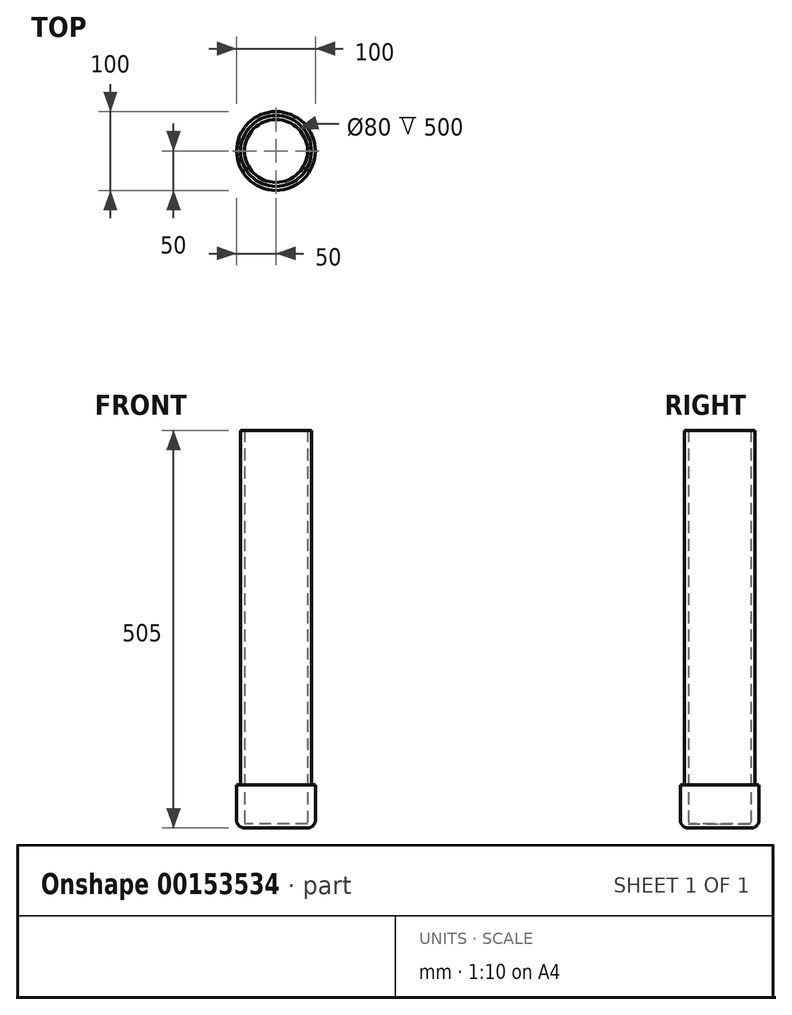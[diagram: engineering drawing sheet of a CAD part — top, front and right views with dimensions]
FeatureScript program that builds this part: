
annotation { "Feature Type Name" : "Feature", "Feature Type Description" : "" }
export const myFeature = defineFeature(function(context is Context, id is Id, definition is map)
    precondition{}
    {
        {
            var Q0;
            Q0=qCreatedBy(makeId("Top.planeOp"),FACE);
            var sketch = newSketch(context, id + "F0", { "sketchPlane" : qUnion([Q0])});
            skCircle(sketch, "E0", {"center": v(0, 0) * mm, "radius": 40 * mm});
            skCircle(sketch, "E1", {"center": v(0, 0) * mm, "radius": 50 * mm});
            skCircle(sketch, "E2", {"center": v(0, 0) * mm, "radius": 45 * mm});
            skSolve(sketch);
        }
        {
            var Q0;
            Q0=makeQuery(id+"F0.imprint","IMPRINT",FACE,{"disambiguationData":[TD([[makeQuery(id+"F0.imprint","IMPRINT",EDGE,{"derivedFrom":sQuery(id+"F0.wireOp",EDGE,"E0")}),-1.0]])]});
            extrude(context, id + "F1", {"entities" : qUnion([Q0]), "depth" : 500 * mm});
        }
        {
            var Q0;
            Q0=makeQuery(id+"F0.imprint","IMPRINT",FACE,{"disambiguationData":[TD([[makeQuery(id+"F0.imprint","IMPRINT",EDGE,{"derivedFrom":sQuery(id+"F0.wireOp",EDGE,"E1")}),1.0]])]});
            extrude(context, id + "F2", {"entities" : qUnion([Q0]), "operationType" : NewBodyOperationType.ADD, "depth" : 50 * mm});
        }
        {
            var Q0;
            Q0=makeQuery(id+"F2.opExtrude","CAP_FACE",FACE,{"disambiguationData":[OSD([sQuery(id+"F0.wireOp",EDGE,"E1"),sQuery(id+"F0.wireOp",EDGE,"E2")])],"isStart":false});
            var Q1;
            Q1=makeQuery(id+"F1.opExtrude","CAP_FACE",FACE,{"disambiguationData":[OSD([sQuery(id+"F0.wireOp",EDGE,"E0"),sQuery(id+"F0.wireOp",EDGE,"E2")])],"isStart":false});
            var Q2;
            Q2=makeQuery(id+"F0.imprint","IMPRINT",FACE,{"disambiguationData":[TD([[makeQuery(id+"F0.imprint","IMPRINT",EDGE,{"derivedFrom":sQuery(id+"F0.wireOp",EDGE,"E0")}),1.0]])]});
            extrude(context, id + "F3", {"entities" : qUnion([Q0, Q1, Q2]), "operationType" : NewBodyOperationType.ADD, "depth" : 5 * mm});
        }
        {
            var Q0;
            Q0=makeQuery(id+"F2.opExtrude","CAP_EDGE",EDGE,{"disambiguationData":[OSD([sQuery(id+"F0.wireOp",EDGE,"E1")])],"isStart":true});
            fillet(context, id + "F4", {"entities" : qUnion([Q0]), "radius" : 10 * mm, "tangentPropagation" : true, "allowEdgeOverflow" : false});
        }
    });
